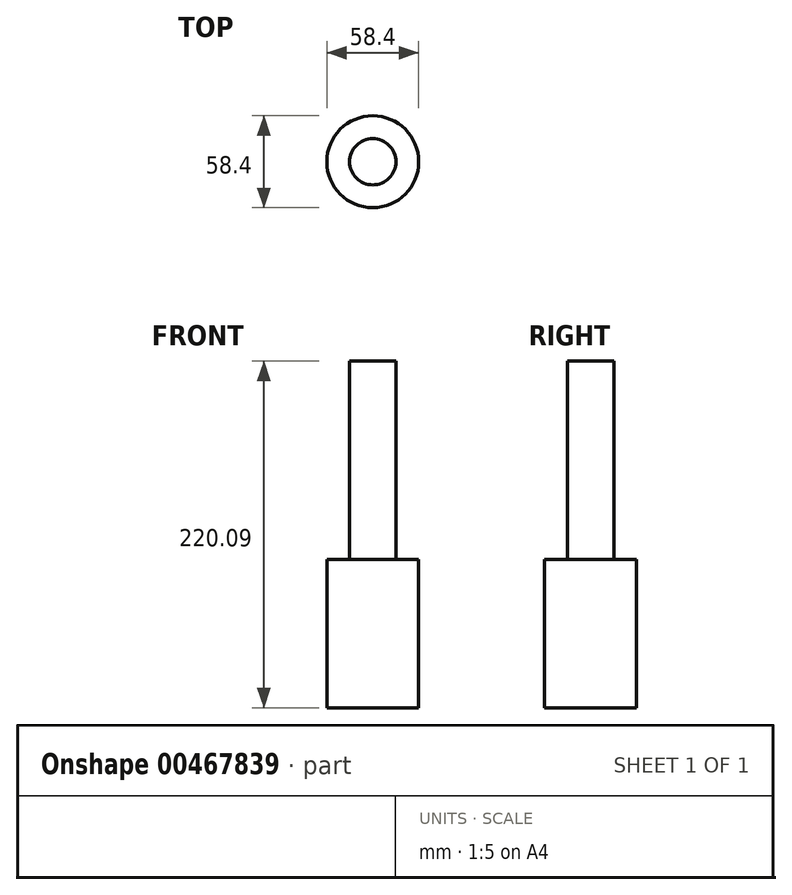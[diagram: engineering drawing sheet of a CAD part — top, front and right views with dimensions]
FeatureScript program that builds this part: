
annotation { "Feature Type Name" : "Feature", "Feature Type Description" : "" }
export const myFeature = defineFeature(function(context is Context, id is Id, definition is map)
    precondition{}
    {
        {
            var Q0;
            Q0=qCreatedBy(makeId("Top.planeOp"),FACE);
            var sketch = newSketch(context, id + "F0", { "sketchPlane" : qUnion([Q0])});
            skCircle(sketch, "E0", {"center": v(0, 0) * mm, "radius": 29.2 * mm});
            skSolve(sketch);
        }
        {
            var Q0;
            Q0 = qSketchRegion(id + "F0", true);
            extrude(context, id + "F1", {"entities" : qUnion([Q0]), "depth" : 94.28 * mm, "symmetric" : true});
        }
        {
            var Q0;
            Q0=makeQuery(id+"F1.opExtrude","CAP_FACE",FACE,{"disambiguationData":[OSD([sQuery(id+"F0.wireOp",EDGE,"E0")])],"isStart":false});
            var sketch = newSketch(context, id + "F2", { "sketchPlane" : qUnion([Q0])});
            skCircle(sketch, "E1", {"center": v(0, 0) * mm, "radius": 14.72 * mm});
            skSolve(sketch);
        }
        {
            var Q0;
            Q0 = qSketchRegion(id + "F2", true);
            extrude(context, id + "F3", {"entities" : qUnion([Q0]), "operationType" : NewBodyOperationType.ADD, "depth" : 125.81 * mm});
        }
    });
